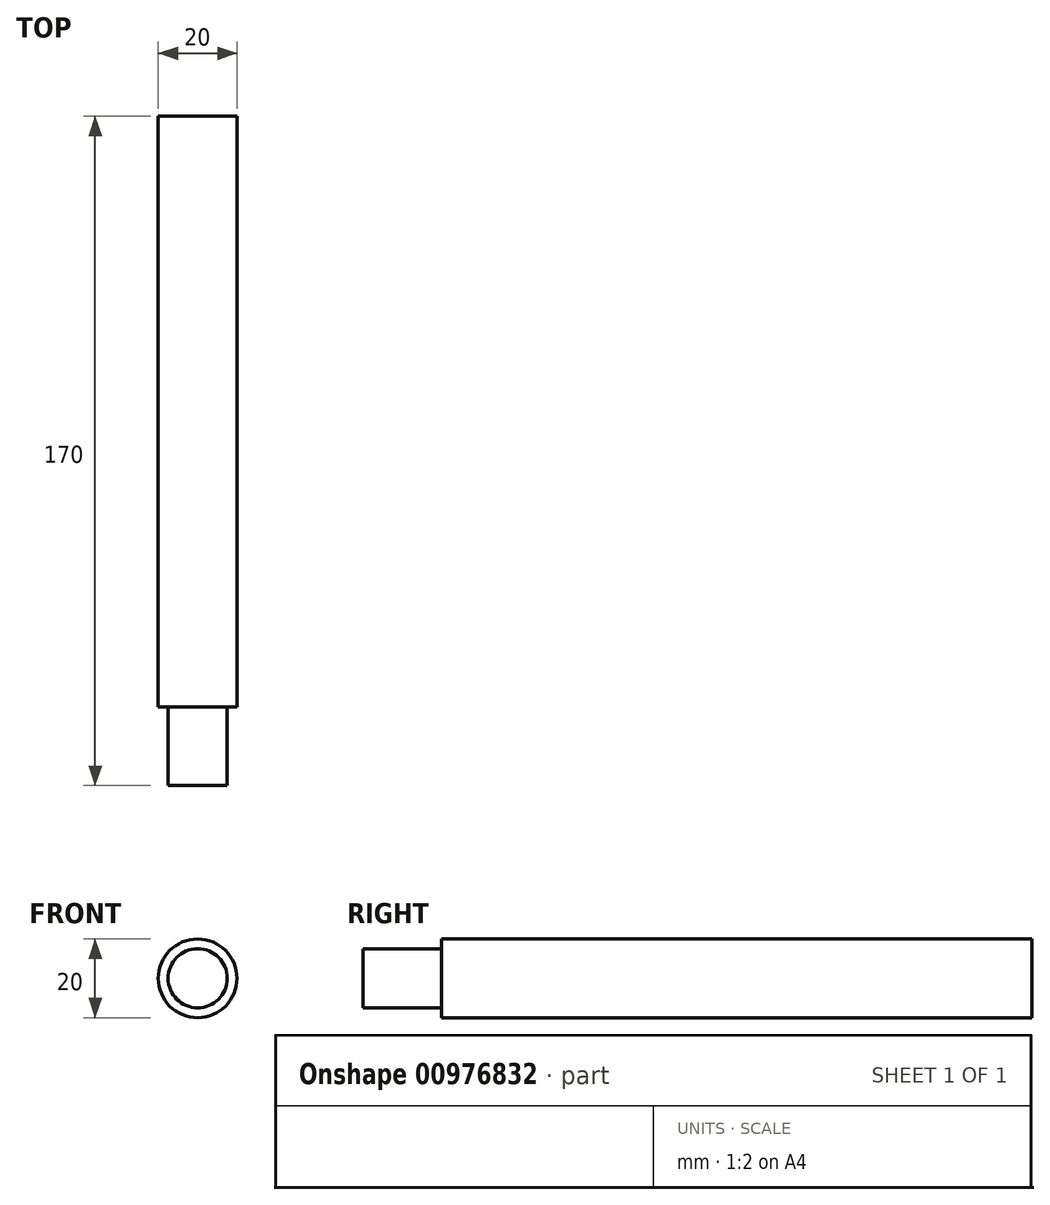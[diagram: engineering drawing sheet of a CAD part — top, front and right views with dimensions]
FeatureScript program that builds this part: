
annotation { "Feature Type Name" : "Feature", "Feature Type Description" : "" }
export const myFeature = defineFeature(function(context is Context, id is Id, definition is map)
    precondition{}
    {
        {
            var Q0;
            Q0=qCreatedBy(makeId("Right.planeOp"),FACE);
            var sketch = newSketch(context, id + "F0", { "sketchPlane" : qUnion([Q0])});
            skLineSegment(sketch, "E0", {"start": v(0, 0) * mm, "end": v(0, 7.5) * mm});
            skLineSegment(sketch, "E1", {"start": v(0, 7.5) * mm, "end": v(20, 7.5) * mm});
            skLineSegment(sketch, "E2", {"start": v(20, 10) * mm, "end": v(170, 10) * mm});
            skLineSegment(sketch, "E3", {"start": v(170, 10) * mm, "end": v(170, 0) * mm});
            skLineSegment(sketch, "E4", {"start": v(170, 0) * mm, "end": v(0, 0) * mm});
            skLineSegment(sketch, "E5", {"start": v(20, 7.5) * mm, "end": v(20, 10) * mm});
            skSolve(sketch);
        }
        {
            var Q0;
            Q0 = qSketchRegion(id + "F0", true);
            var Q1;
            Q1=sQuery(id+"F0.wireOp",EDGE,"E4");
            revolve(context, id + "F1", {"surfaceOperationType" : NewSurfaceOperationType.NEW, "entities" : qUnion([Q0]), "axis" : qUnion([Q1]), "revolveType" : RevolveType.FULL});
        }
    });
